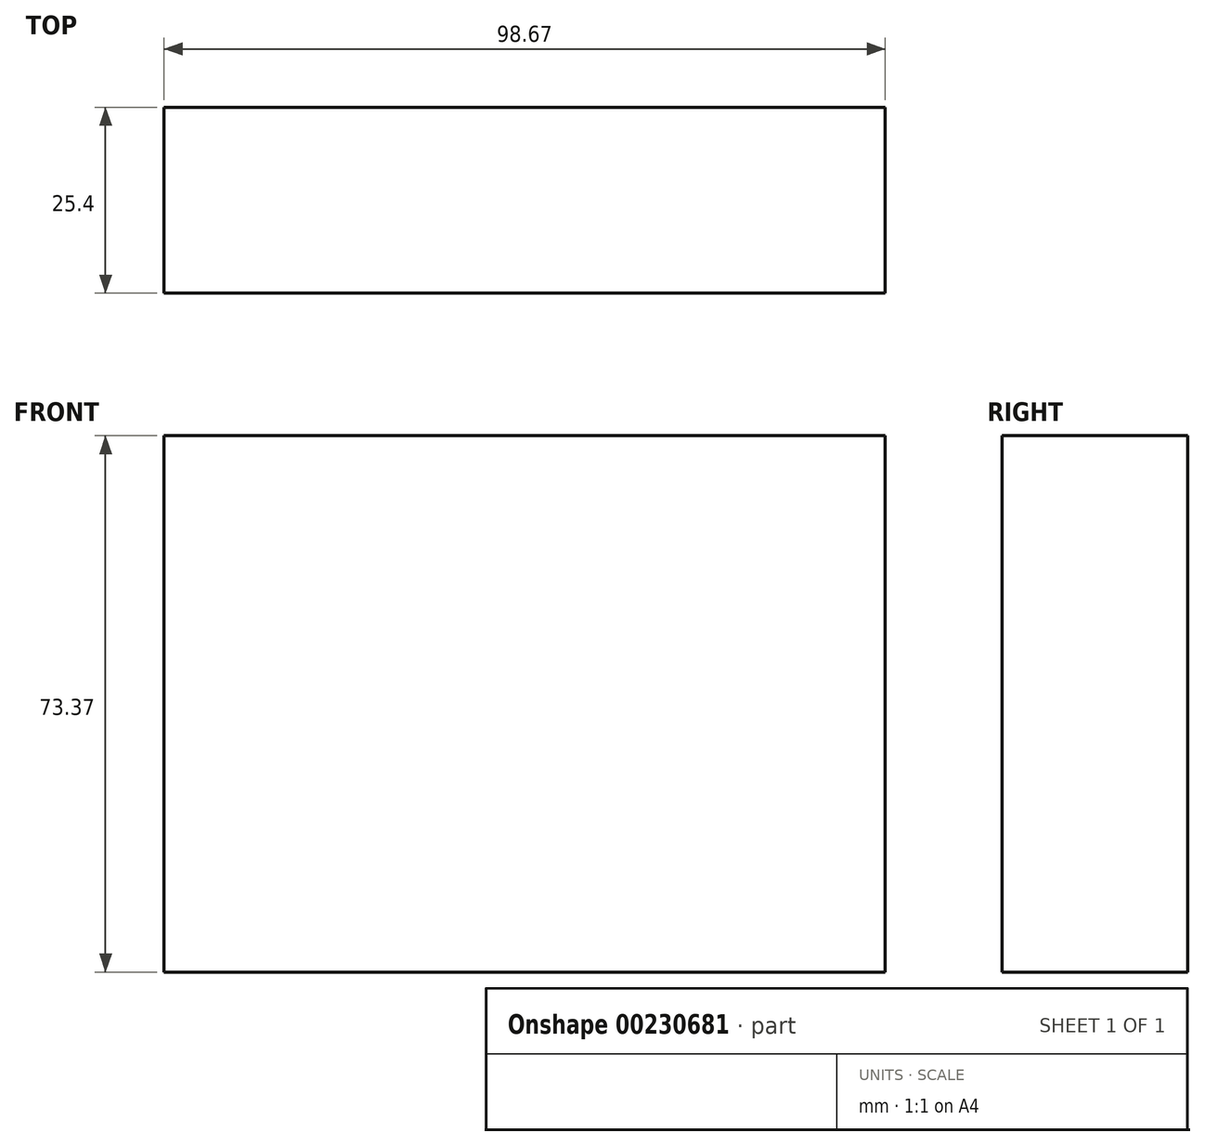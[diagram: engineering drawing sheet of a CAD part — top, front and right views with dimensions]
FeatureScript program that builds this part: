
annotation { "Feature Type Name" : "Feature", "Feature Type Description" : "" }
export const myFeature = defineFeature(function(context is Context, id is Id, definition is map)
    precondition{}
    {
        {
            var Q0;
            Q0=qCreatedBy(makeId("Front.planeOp"),FACE);
            var sketch = newSketch(context, id + "F0", { "sketchPlane" : qUnion([Q0])});
            skLineSegment(sketch, "E0.bottom", {"start": v(-46.01, 37.58) * mm, "end": v(52.66, 37.58) * mm});
            skLineSegment(sketch, "E0.top", {"start": v(-46.01, -35.79) * mm, "end": v(52.66, -35.79) * mm});
            skLineSegment(sketch, "E0.left", {"start": v(-46.01, 37.58) * mm, "end": v(-46.01, -35.79) * mm});
            skLineSegment(sketch, "E0.right", {"start": v(52.66, 37.58) * mm, "end": v(52.66, -35.79) * mm});
            skSolve(sketch);
        }
        {
            var Q0;
            Q0=makeQuery(id+"F0.imprint","IMPRINT",FACE,{"disambiguationData":[TD([[makeQuery(id+"F0.imprint","IMPRINT",EDGE,{"derivedFrom":sQuery(id+"F0.wireOp",EDGE,"E0.bottom")}),-1.0]])]});
            extrude(context, id + "F1", {"entities" : qUnion([Q0]), "depth" : 25.4 * mm});
        }
    });
